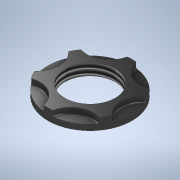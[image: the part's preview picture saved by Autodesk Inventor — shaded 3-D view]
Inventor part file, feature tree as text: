
AUTODESK INVENTOR PART (.ipt)
format: ipt  version: 2020 (Build 240168000, 168)  size: 212,992 bytes
history: native  units: mm
features: extrude x2, sketch x1, pattern_circular x1, fillet x1, thread x1
ambient origin geometry x8: Origin, YZ Plane, XZ Plane, XY Plane, X Axis, Y Axis, Z Axis, Center Point
bodies: Solid1 (feature_tree)
feature tree (6):
  sketch  "Sketch1"  dims[d0=45.0mm d1=75.0mm d2=40.0mm d3=47.5mm d4=10.0mm d5=0.0mm d6=5.0mm d7=0.0mm d8=60.0mm d9=360.0deg d11=1.0mm d12=10.0mm d13=0.0mm]
  extrude  "Extrusion1"  Depth=1.0mm
  extrude  "Extrusion2"  Depth=1.0mm
  pattern_circular  "Circular Pattern1"  [2 undecoded]
  fillet  "Fillet1"  Radius=10.0mm
  thread  "Thread1"  [1 undecoded]
note: 3 required parameter values undecoded (feature->parameter linkage not recoverable at this tier; creation-order binding heuristic only, values carry confidence <= 0.55)
